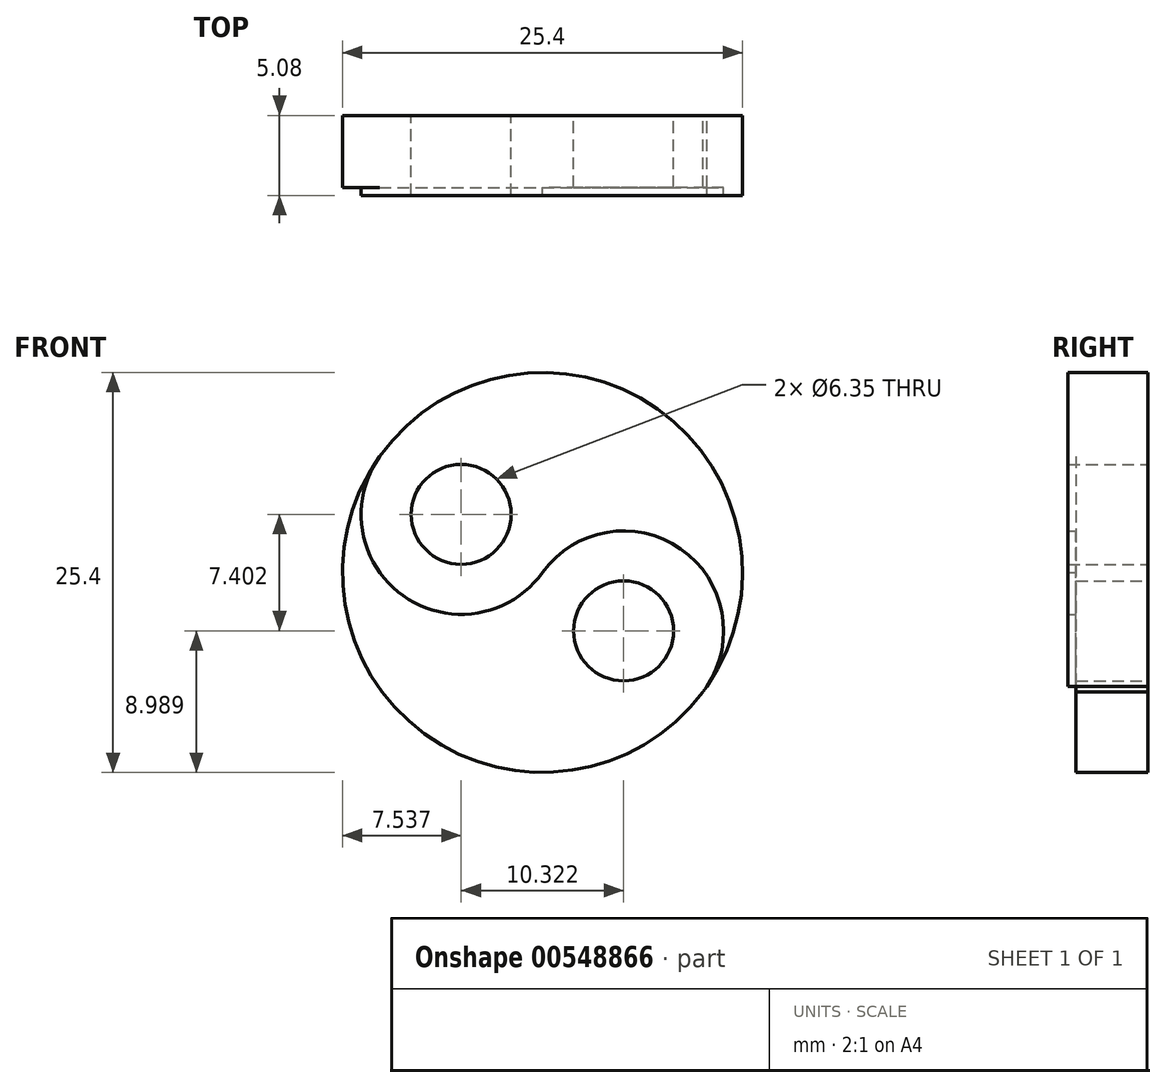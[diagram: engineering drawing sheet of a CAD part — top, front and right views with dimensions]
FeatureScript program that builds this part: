
annotation { "Feature Type Name" : "Feature", "Feature Type Description" : "" }
export const myFeature = defineFeature(function(context is Context, id is Id, definition is map)
    precondition{}
    {
        {
            var Q0;
            Q0=qCreatedBy(makeId("Front.planeOp"),FACE);
            var sketch = newSketch(context, id + "F0", { "sketchPlane" : qUnion([Q0])});
            skCircle(sketch, "E0", {"center": v(-17.43, -15.89) * mm, "radius": 12.7 * mm});
            skArc(sketch, "E1", {"start": v(-7.02, -23.17) * mm, "mid": v(-7, -23.13) * mm, "end": v(-6.97, -23.1) * mm});
            skArc(sketch, "E2", {"start": v(-7.25, -23.49) * mm, "mid": v(-8.47, -14.51) * mm, "end": v(-17.42, -15.9) * mm});
            skLineSegment(sketch, "E3", {"start": v(-27.76, -8.5) * mm, "end": v(-27.76, -8.5) * mm});
            skArc(sketch, "E4", {"start": v(-27.76, -8.5) * mm, "mid": v(-26.28, -17.37) * mm, "end": v(-17.43, -15.89) * mm});
            skCircle(sketch, "E5", {"center": v(-22.6, -12.2) * mm, "radius": 3.18 * mm});
            skCircle(sketch, "E6", {"center": v(-12.27, -19.6) * mm, "radius": 3.18 * mm});
            skLineSegment(sketch, "E7", {"start": v(-17.43, -15.89) * mm, "end": v(-17.42, -15.9) * mm});
            skSolve(sketch);
        }
        {
            var Q0;
            {var subQ5=sQuery(id+"F0.wireOp",EDGE,"E4");Q0=makeQuery(id+"F0.imprint","IMPRINT",FACE,{"disambiguationData":[TD([[makeQuery(id+"F0.imprint","IMPRINT",EDGE,{"derivedFrom":subQ5}),1.0]])]});}
            extrude(context, id + "F1", {"entities" : qUnion([Q0]), "depth" : 5.08 * mm, "offsetDistance" : 25.4 * mm});
        }
        {
            var Q0;
            Q0 = qSketchRegion(id + "F0", true);
            extrude(context, id + "F2", {"entities" : qUnion([Q0]), "operationType" : NewBodyOperationType.ADD, "depth" : 4.57 * mm, "offsetDistance" : 25.4 * mm});
        }
    });
